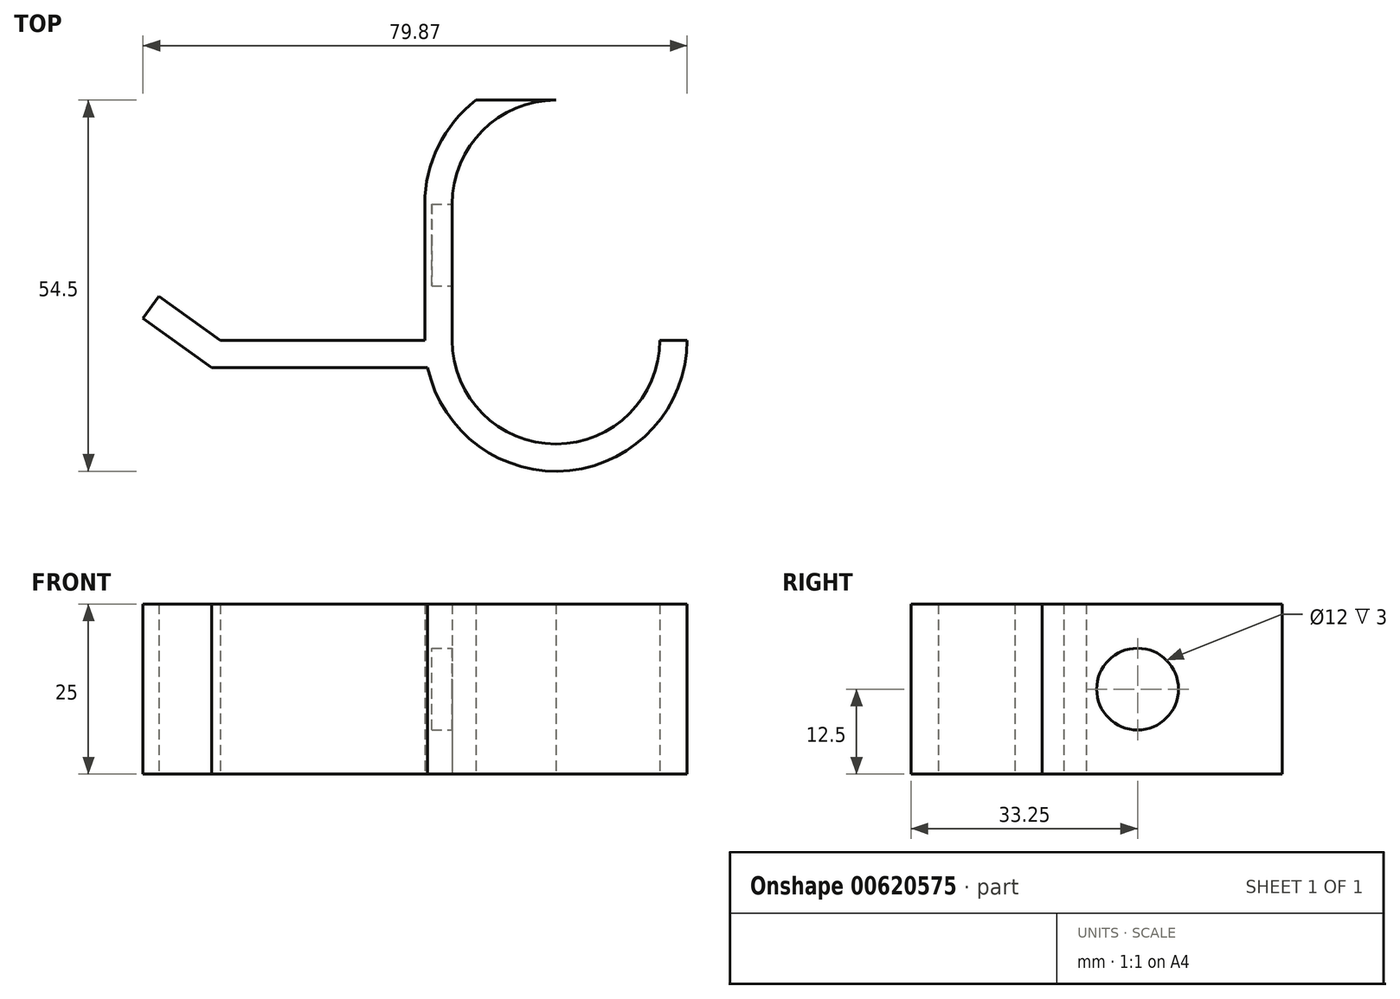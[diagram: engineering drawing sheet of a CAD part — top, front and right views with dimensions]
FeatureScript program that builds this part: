
annotation { "Feature Type Name" : "Feature", "Feature Type Description" : "" }
export const myFeature = defineFeature(function(context is Context, id is Id, definition is map)
    precondition{}
    {
        {
            var Q0;
            Q0=qCreatedBy(makeId("Top.planeOp"),FACE);
            var sketch = newSketch(context, id + "F0", { "sketchPlane" : qUnion([Q0])});
            skLineSegment(sketch, "E0", {"start": v(0, 0) * mm, "end": v(0, 20) * mm});
            skArc(sketch, "E1", {"start": v(30.5, 20) * mm, "mid": v(15.25, 35.25) * mm, "end": v(0, 20) * mm});
            skLineSegment(sketch, "E2", {"start": v(30.5, 20) * mm, "end": v(30.5, 0) * mm});
            skArc(sketch, "E3", {"start": v(0, 0) * mm, "mid": v(15.25, -15.25) * mm, "end": v(30.5, 0) * mm});
            skArc(sketch, "E4.0", {"start": v(-4, 0) * mm, "mid": v(15.25, -19.25) * mm, "end": v(34.5, 0) * mm});
            skLineSegment(sketch, "E4.1", {"start": v(-4, 0) * mm, "end": v(-4, 20) * mm});
            skArc(sketch, "E4.2", {"start": v(3.5, 35.25) * mm, "mid": v(-2.02, 28.5) * mm, "end": v(-4, 20) * mm});
            skLineSegment(sketch, "E5", {"start": v(15.25, 35.25) * mm, "end": v(3.5, 35.25) * mm});
            skLineSegment(sketch, "E6", {"start": v(30.5, 0) * mm, "end": v(34.5, 0) * mm});
            skLineSegment(sketch, "E7", {"start": v(-4, 0) * mm, "end": v(-34, 0) * mm});
            skLineSegment(sketch, "E8", {"start": v(-34, 0) * mm, "end": v(-43.05, 6.45) * mm});
            skLineSegment(sketch, "E9.0", {"start": v(-35.28, -4) * mm, "end": v(-45.37, 3.2) * mm});
            skLineSegment(sketch, "E9.1", {"start": v(-3.58, -4) * mm, "end": v(-35.28, -4) * mm});
            skLineSegment(sketch, "E10", {"start": v(-45.37, 3.2) * mm, "end": v(-43.05, 6.45) * mm});
            skSolve(sketch);
        }
        {
            var Q0;
            {var subQ0=sQuery(id+"F0.wireOp",EDGE,"E7");Q0=makeQuery(id+"F0.imprint","IMPRINT",FACE,{"disambiguationData":[TD([[makeQuery(id+"F0.imprint","IMPRINT",EDGE,{"derivedFrom":subQ0}),1.0]])]});}
            var Q1;
            {var subQ1=sQuery(id+"F0.wireOp",EDGE,"E0");Q1=makeQuery(id+"F0.imprint","IMPRINT",FACE,{"disambiguationData":[TD([[makeQuery(id+"F0.imprint","IMPRINT",EDGE,{"derivedFrom":subQ1}),1.0]])]});}
            extrude(context, id + "F1", {"entities" : qUnion([Q0, Q1]), "depth" : 25 * mm, "offsetDistance" : 25 * mm});
        }
        {
            var Q0;
            Q0=makeQuery(id+"F1.opExtrude","SWEPT_FACE",FACE,{"disambiguationData":[OSD([sQuery(id+"F0.wireOp",EDGE,"E0")])]});
            var sketch = newSketch(context, id + "F2", { "sketchPlane" : qUnion([Q0])});
            skLineSegment(sketch, "E11", {"start": v(20, 12.5) * mm, "end": v(14, 12.5) * mm});
            skCircle(sketch, "E12", {"center": v(14, 12.5) * mm, "radius": 6 * mm});
            skSolve(sketch);
        }
        {
            var Q0;
            Q0 = qSketchRegion(id + "F2", true);
            extrude(context, id + "F3", {"entities" : qUnion([Q0]), "operationType" : NewBodyOperationType.REMOVE, "oppositeDirection" : true, "depth" : 3 * mm, "offsetDistance" : 25 * mm});
        }
    });
